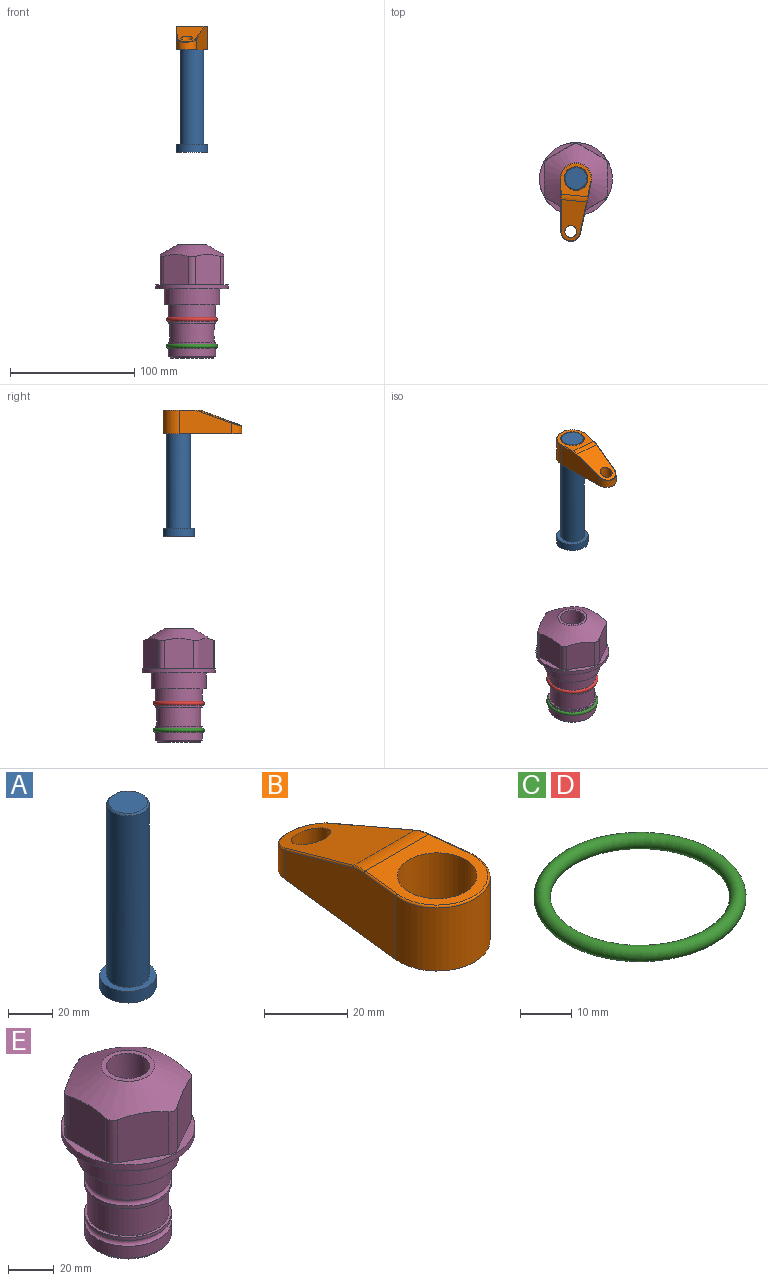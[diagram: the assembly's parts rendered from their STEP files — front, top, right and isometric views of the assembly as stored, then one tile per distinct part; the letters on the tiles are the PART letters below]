
ASSEMBLY  parts=5 mates=3
PART A: 6 faces, bbox 25.4x25.4x101.6 mm
  f0: plane 17.46x17.46mm, normal (0,0,1), area 239.5mm2, adj f5
  f1: plane 25.4x25.4mm, normal (0,0,-1), area 506.7mm2, adj f2
  f2: cylinder r=12.7mm len=25.4mm, axis (0,0,1), area 506.7mm2, adj f1,f3
  f3: plane 25.4x25.4mm, normal (0,0,1), area 221.7mm2, adj f2,f4
  f4: cylinder r=9.53mm len=94.46mm, axis (0,0,1), area 5653mm2, adj f3,f5
  f5: cone r=8.73mm half-angle=45deg, axis (0,0,-1), area 64.4mm2, adj f0,f4
PART B: 44 faces, bbox 27.5x64.5x19.1 mm
  f0: plane 2.3x0.95mm, normal (0,0,-1), area 1mm2, adj f25,f30,f34
  f1: plane 63.5x25.4mm, normal (0,0,-1), area 561.7mm2, adj f2,f3,f4,f5,f6,f7,f19,f20
  f2: cylinder r=12.7mm len=25.4mm, axis (0,0,-1), area 792.2mm2, adj f1,f3,f5,f13
  f3: plane 42.33x18.54mm, normal (0.99,0.11,0), area 647mm2, adj f1,f2,f4,f11,f12,f14
  f4: cylinder r=7.94mm len=15.78mm, axis (0,0,-1), area 158.6mm2, adj f1,f3,f5,f16
  f5: plane 42.33x18.54mm, normal (-0.99,0.11,0), area 647mm2, adj f1,f2,f4,f15,f17,f18
  f6: cylinder r=9.53mm len=19.05mm, axis (0,0,-1), area 1140.1mm2, adj f1,f8
  f7: cylinder r=4.76mm len=10.98mm, axis (0,0,-1), area 276.1mm2, adj f1,f9
  f8: plane 25.83x24.38mm, normal (0,0,1), area 262.2mm2, adj f6,f10,f11,f13,f15
  f9: plane 32.49x20.55mm, normal (0,0.34,0.94), area 489.9mm2, adj f7,f10,f14,f16,f18
  f10: cylinder r=12.7mm len=21.49mm, axis (-1,0,0), area 93.2mm2, adj f8,f9,f12,f17
  f11: cylinder r=0.51mm len=12.34mm, axis (0.11,-0.99,0), area 9.9mm2, adj f3,f8,f12,f13
  f12: bspline ~7.62x1.64mm, area 3.5mm2, adj f3,f10,f11,f14
  f13: torus R=12.19mm, axis (0,0,1), area 33.6mm2, adj f2,f8,f11,f15
  f14: cylinder r=0.51mm len=26.01mm, axis (0.1,-0.93,0.34), area 21.6mm2, adj f3,f9,f12,f16
  f15: cylinder r=0.51mm len=12.34mm, axis (0.11,0.99,0), area 9.9mm2, adj f5,f8,f13,f17
  f16: bspline ~15.78x7.05mm, area 15.7mm2, adj f4,f9,f14,f18
  f17: bspline ~7.62x1.64mm, area 3.5mm2, adj f5,f10,f15,f18
  f18: cylinder r=0.51mm len=26.01mm, axis (0.1,0.93,-0.34), area 21.6mm2, adj f5,f9,f16,f17
  f19: plane 21.6x14.29mm, normal (-0.99,-0.11,0), area 242.6mm2, adj f1,f26,f28,f34,f36,f38
  f20: plane 21.6x14.29mm, normal (0.99,-0.11,0), area 242.6mm2, adj f1,f27,f29,f37,f39,f41
  f21: cylinder r=12.7mm len=14.29mm, axis (0,0,-1), area 173.2mm2, adj f1,f26,f27,f30,f31,f33
  f22: cylinder r=7.94mm len=7.63mm, axis (0,0,-1), area 53.8mm2, adj f1,f28,f29,f42
  f23: plane 2.3x0.95mm, normal (0,0,-1), area 1mm2, adj f25,f33,f37
  f24: plane 17.94x12.32mm, normal (0,-0.34,-0.94), area 191.2mm2, adj f25,f38,f41,f42
  f25: cylinder r=9.53mm len=12.93mm, axis (-1,0,0), area 37.5mm2, adj f0,f23,f24,f31,f36,f39
  f26: cylinder r=1.59mm len=14.29mm, axis (0,0,-1), area 49mm2, adj f1,f19,f21,f32
  f27: cylinder r=1.59mm len=14.29mm, axis (0,0,-1), area 49mm2, adj f1,f20,f21,f35
  f28: cylinder r=1.59mm len=7.28mm, axis (0,0,-1), area 22.1mm2, adj f1,f19,f22,f40
  f29: cylinder r=1.59mm len=7.28mm, axis (0,0,-1), area 22.1mm2, adj f1,f20,f22,f43
  f30: torus R=14.29mm, axis (0,0,1), area 5.8mm2, adj f0,f21,f31,f32
  f31: bspline ~11.06x2.73mm, area 20.8mm2, adj f21,f25,f30,f33
  f32: sphere r=1.59mm, area 5.4mm2, adj f26,f30,f34
  f33: torus R=14.29mm, axis (0,0,1), area 5.8mm2, adj f21,f23,f31,f35
  f34: cylinder r=1.59mm len=1.68mm, axis (-0.11,0.99,0), area 2.4mm2, adj f0,f19,f32,f36
  f35: sphere r=1.59mm, area 5.4mm2, adj f27,f33,f37
  f36: bspline ~5.82x2.33mm, area 7.7mm2, adj f19,f25,f34,f38
  f37: cylinder r=1.59mm len=1.68mm, axis (0.11,0.99,0), area 2.4mm2, adj f20,f23,f35,f39
  f38: cylinder r=1.59mm len=18.33mm, axis (0.1,-0.93,0.34), area 46.7mm2, adj f19,f24,f36,f40
  f39: bspline ~5.82x2.33mm, area 7.7mm2, adj f20,f25,f37,f41
  f40: sphere r=1.59mm, area 3.6mm2, adj f28,f38,f42
  f41: cylinder r=1.59mm len=18.33mm, axis (0.1,0.93,-0.34), area 46.7mm2, adj f20,f24,f39,f43
  f42: bspline ~8.31x1.84mm, area 15.3mm2, adj f22,f24,f40,f43
  f43: sphere r=1.59mm, area 3.6mm2, adj f29,f41,f42
PART C: 1 faces, bbox 44.7x44.7x3.2 mm
  f0: torus R=19.05mm, axis (0,0,1), area 1193.9mm2
PART D: same geometry as C
PART E: 36 faces, bbox 58.7x58.7x91.2 mm
  f0: cylinder r=17.78mm len=35.56mm, axis (0,0,1), area 1670.8mm2, adj f23,f24,f31
  f1: cylinder r=19.05mm len=38.1mm, axis (0,0,1), area 1191.9mm2, adj f26,f27,f30
  f2: plane 58.66x58.66mm, normal (0,0,-1), area 1150.6mm2, adj f3,f28
  f3: cylinder r=29.33mm len=58.66mm, axis (0,0,-1), area 585.1mm2, adj f2,f4
  f4: plane 58.66x58.66mm, normal (0,0,1), area 475.9mm2, adj f3,f5,f6,f7,f8,f9,f10,f11
  f5: plane 24.5x20.32mm, normal (-0.5,0.87,0), area 562.8mm2, adj f4,f15,f16,f17
  f6: plane 24.5x20.32mm, normal (0.5,0.87,0), area 562.8mm2, adj f4,f14,f15,f17
  f7: plane 24.5x23.48mm, normal (1,0,0), area 562.8mm2, adj f4,f13,f14,f17
  f8: plane 24.5x20.32mm, normal (0.5,-0.87,0), area 562.8mm2, adj f4,f12,f13,f17
  f9: plane 24.5x20.32mm, normal (-0.5,-0.87,0), area 562.8mm2, adj f4,f11,f12,f17
  f10: plane 24.5x23.48mm, normal (-1,0,0), area 562.8mm2, adj f4,f11,f16,f17
  f11: cylinder r=5.08mm len=23.01mm, axis (0,0,-1), area 121.2mm2, adj f4,f9,f10,f17
  f12: cylinder r=5.08mm len=23.01mm, axis (0,0,-1), area 121.2mm2, adj f4,f8,f9,f17
  f13: cylinder r=5.08mm len=23.01mm, axis (0,0,-1), area 121.2mm2, adj f4,f7,f8,f17
  f14: cylinder r=5.08mm len=23.01mm, axis (0,0,-1), area 121.2mm2, adj f4,f6,f7,f17
  f15: cylinder r=5.08mm len=23.01mm, axis (0,0,-1), area 121.2mm2, adj f4,f5,f6,f17
  f16: cylinder r=5.08mm len=23.01mm, axis (0,0,-1), area 121.2mm2, adj f4,f5,f10,f17
  f17: cone r=11.73mm half-angle=60deg, axis (0,0,-1), area 2071.8mm2, adj f5,f6,f7,f8,f9,f10,f11,f12
  f18: plane 23.46x23.46mm, normal (0,0,1), area 147.4mm2, adj f17,f35
  f19: plane 34.93x34.93mm, normal (0,0,-1), area 958mm2, adj f29
  f20: cylinder r=19.05mm len=38.1mm, axis (0,0,1), area 760.1mm2, adj f21,f29
  f21: torus R=19.05mm, axis (0,0,1), area 565.3mm2, adj f20,f22
  f22: cylinder r=19.05mm len=38.1mm, axis (0,0,1), area 190mm2, adj f21,f23
  f23: plane 38.1x38.1mm, normal (0,0,1), area 146.9mm2, adj f0,f22
  f24: plane 38.1x38.1mm, normal (0,0,-1), area 146.9mm2, adj f0,f25
  f25: cylinder r=19.05mm len=38.1mm, axis (0,0,1), area 190mm2, adj f24,f26
  f26: torus R=19.05mm, axis (0,0,1), area 565.3mm2, adj f1,f25
  f27: plane 44.45x44.45mm, normal (0,0,-1), area 411.7mm2, adj f1,f28
  f28: cylinder r=22.23mm len=44.45mm, axis (0,0,1), area 1773.5mm2, adj f2,f27
  f29: cone r=19.05mm half-angle=45deg, axis (0,0,1), area 257.5mm2, adj f19,f20
  f30: cylinder r=3.17mm len=6.75mm, axis (-1,0,0), area 128mm2, adj f1,f33
  f31: cylinder r=3.17mm len=6.35mm, axis (-1,0,0), area 102.5mm2, adj f0,f33
  f32: plane 25.4x25.4mm, normal (0,0,1), area 506.7mm2, adj f33
  f33: cylinder r=12.7mm len=66.42mm, axis (0,0,-1), area 5236.2mm2, adj f30,f31,f32,f34
  f34: cone r=9.53mm half-angle=30deg, axis (0,0,-1), area 443.4mm2, adj f33,f35
  f35: cylinder r=9.53mm len=19.05mm, axis (0,0,-1), area 849mm2, adj f18,f34
PLACE A rot(axis=(0,0,-1),95.6deg) t=(0,0,138.07)mm
PLACE B rot(axis=(0,0,1),174.4deg) t=(0,0,192.68)mm
PLACE C t=(0,0,-21.59)mm
PLACE D at identity
PLACE E at identity fixed
MATE fastened C.f0 <-> E.f0  axis (0,0,1) through (0,0,-46.1)mm
MATE cylindrical A.f2 <-> E.f0  axis (0,0,1) through (0,0,163.71)mm
MATE fastened B.f2 <-> A.f2  axis (0,0,1) through (0,0,211.73)mm
